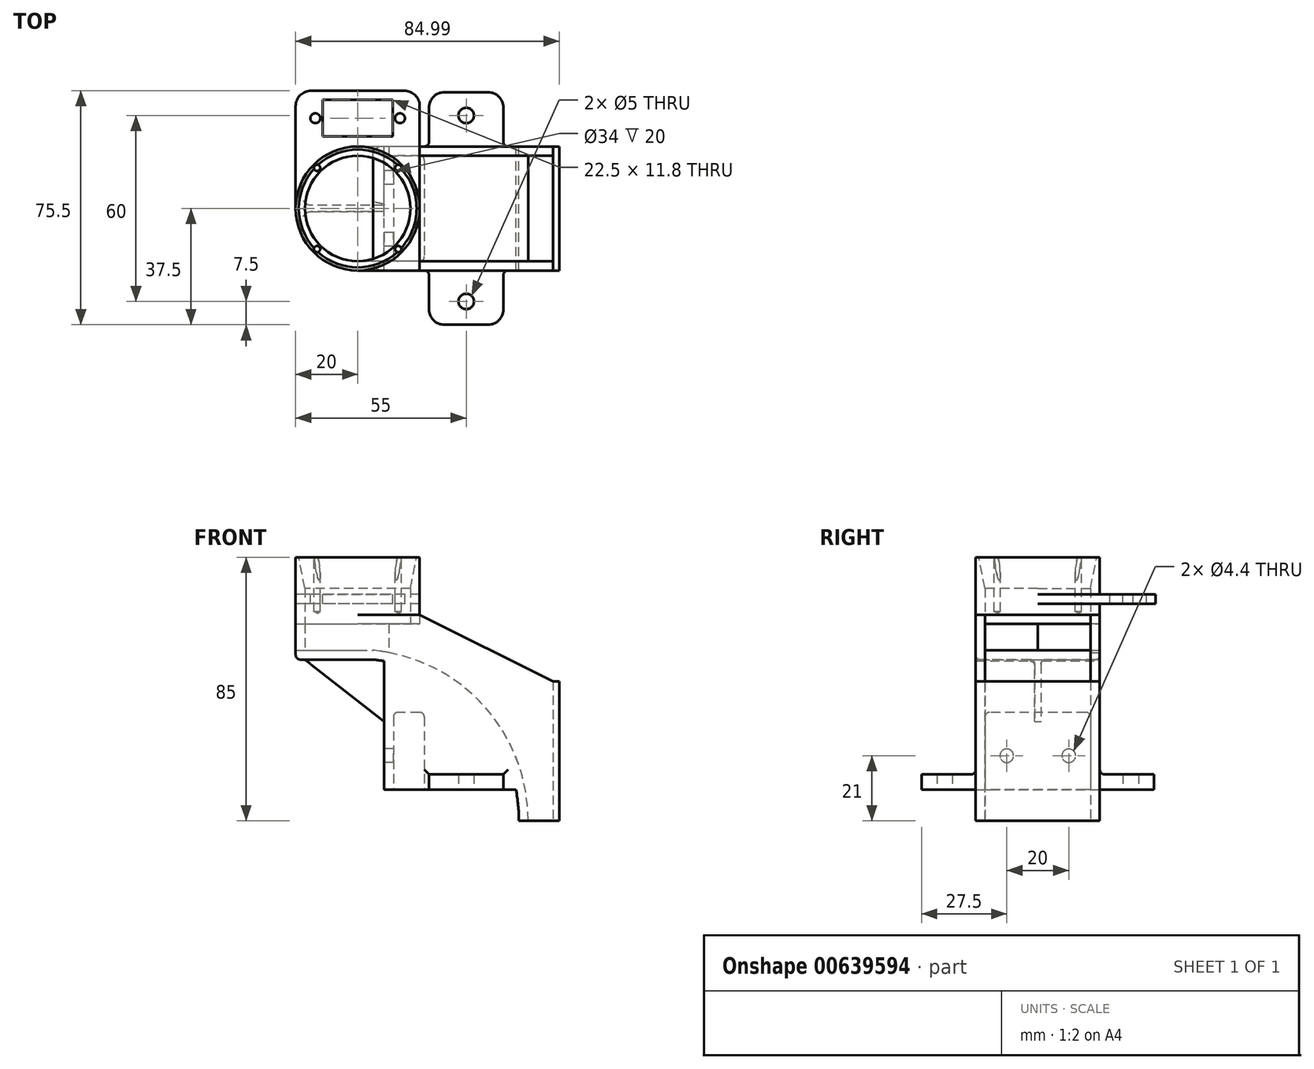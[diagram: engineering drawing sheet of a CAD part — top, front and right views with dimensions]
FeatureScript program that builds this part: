
annotation { "Feature Type Name" : "Feature", "Feature Type Description" : "" }
export const myFeature = defineFeature(function(context is Context, id is Id, definition is map)
    precondition{}
    {
        {
            var Q0;
            Q0=qCreatedBy(makeId("Top.planeOp"),FACE);
            var sketch = newSketch(context, id + "F0", { "sketchPlane" : qUnion([Q0])});
            skCircle(sketch, "E0", {"center": v(0, 0) * mm, "radius": 17 * mm});
            skCircle(sketch, "E1", {"center": v(0, 0) * mm, "radius": 20 * mm});
            skSolve(sketch);
        }
        {
            var Q0;
            Q0 = qSketchRegion(id + "F0", true);
            extrude(context, id + "F1", {"entities" : qUnion([Q0]), "depth" : 30 * mm, "offsetDistance" : 25 * mm});
        }
        {
            var Q0;
            Q0=makeQuery(id+"F1.opExtrude","CAP_EDGE",EDGE,{"disambiguationData":[OSD([sQuery(id+"F0.wireOp",EDGE,"E0")])],"isStart":false});
            chamfer(context, id + "F2", {"entities" : qUnion([Q0]), "chamferType" : ChamferType.TWO_OFFSETS, "width1" : 10 * mm, "oppositeDirection" : false, "width2" : 2 * mm, "tangentPropagation" : true});
        }
        {
            var Q0;
            Q0=makeQuery(id+"F1.opExtrude","CAP_FACE",FACE,{"disambiguationData":[OSD([sQuery(id+"F0.wireOp",EDGE,"E0"),sQuery(id+"F0.wireOp",EDGE,"E1")])],"isStart":false});
            var sketch = newSketch(context, id + "F3", { "sketchPlane" : qUnion([Q0])});
            skPoint(sketch, "E2", {"position": v(-13.08, -13.08) * mm});
            skLineSegment(sketch, "E3", {"start": v(-13.08, -13.08) * mm, "end": v(0, 0) * mm, "construction": true});
            skPoint(sketch, "E4", {"position": v(-13.08, 13.08) * mm});
            skLineSegment(sketch, "E5", {"start": v(-13.08, 13.08) * mm, "end": v(0, 0) * mm, "construction": true});
            skPoint(sketch, "E6", {"position": v(13.08, 13.08) * mm});
            skPoint(sketch, "E7", {"position": v(13.08, -13.08) * mm});
            skLineSegment(sketch, "E8", {"start": v(13.08, -13.08) * mm, "end": v(0, 0) * mm, "construction": true});
            skLineSegment(sketch, "E9", {"start": v(0, 0) * mm, "end": v(13.08, 13.08) * mm, "construction": true});
            skSolve(sketch);
        }
        {
            var Q0;
            Q0=sQuery(id+"F3.wireOp",VERTEX,"E4");
            var Q1;
            Q1=sQuery(id+"F3.wireOp",VERTEX,"E2");
            var Q2;
            Q2=sQuery(id+"F3.wireOp",VERTEX,"E7");
            var Q3;
            Q3=sQuery(id+"F3.wireOp",VERTEX,"E6");
            var Q4;
            Q4=makeQuery(id+"F1.opExtrude","SWEPT_BODY",BODY,{"disambiguationData":[OSD([sQuery(id+"F0.wireOp",EDGE,"E0"),sQuery(id+"F0.wireOp",EDGE,"E1")])]});
            hole(context, id + "F4", {"style" : HoleStyle.SIMPLE, "endStyle" : HoleEndStyle.BLIND, "holeDiameter" : 2 * mm, "majorDiameter" : 5 * mm, "holeDepth" : 10 * mm, "isTappedThrough" : true, "tappedDepth" : 12 * mm, "tapClearance" : 3, "locations" : qUnion([Q0, Q1, Q2, Q3]), "scope" : qUnion([Q4])});
        }
        {
            var Q0;
            Q0=makeQuery(id+"F1.opExtrude","CAP_FACE",FACE,{"disambiguationData":[OSD([sQuery(id+"F0.wireOp",EDGE,"E0"),sQuery(id+"F0.wireOp",EDGE,"E1")])],"isStart":true});
            var sketch = newSketch(context, id + "F5", { "sketchPlane" : qUnion([Q0])});
            skLineSegment(sketch, "E10", {"start": v(-20, 0) * mm, "end": v(0, 0) * mm});
            skLineSegment(sketch, "E11", {"start": v(0, 0) * mm, "end": v(0, 20) * mm});
            skLineSegment(sketch, "E12", {"start": v(0, 20) * mm, "end": v(20, 20) * mm});
            skLineSegment(sketch, "E13", {"start": v(20, 20) * mm, "end": v(20, -20) * mm});
            skLineSegment(sketch, "E14", {"start": v(20, -20) * mm, "end": v(-20, -20) * mm});
            skLineSegment(sketch, "E15", {"start": v(-20, -20) * mm, "end": v(-20, 0) * mm});
            skSolve(sketch);
        }
        {
            var Q0;
            Q0 = qSketchRegion(id + "F5", true);
            extrude(context, id + "F6", {"entities" : qUnion([Q0]), "operationType" : NewBodyOperationType.REMOVE, "oppositeDirection" : true, "depth" : 8.5 * mm, "offsetDistance" : 25 * mm});
        }
        {
            var Q0;
            Q0=makeQuery(id+"F6.boolean.opBoolean","COPY",FACE,{"derivedFrom":makeQuery(id+"F6.opExtrude","CAP_FACE",FACE,{"disambiguationData":[OSD([sQuery(id+"F5.wireOp",EDGE,"E10"),sQuery(id+"F5.wireOp",EDGE,"E11"),sQuery(id+"F5.wireOp",EDGE,"E12"),sQuery(id+"F5.wireOp",EDGE,"E13"),sQuery(id+"F5.wireOp",EDGE,"E14"),sQuery(id+"F5.wireOp",EDGE,"E15")])],"isStart":false})});
            var sketch = newSketch(context, id + "F7", { "sketchPlane" : qUnion([Q0])});
            skLineSegment(sketch, "E16", {"start": v(0, 20) * mm, "end": v(20, 20) * mm});
            skLineSegment(sketch, "E17", {"start": v(20, 20) * mm, "end": v(20, -20) * mm});
            skLineSegment(sketch, "E18", {"start": v(20, -20) * mm, "end": v(0, -20) * mm});
            skArc(sketch, "E19", {"start": v(0, -20) * mm, "mid": v(20, 0) * mm, "end": v(0, 20) * mm});
            skSolve(sketch);
        }
        {
            var Q0;
            Q0 = qSketchRegion(id + "F7", true);
            extrude(context, id + "F8", {"entities" : qUnion([Q0]), "operationType" : NewBodyOperationType.ADD, "oppositeDirection" : true, "depth" : 3 * mm, "offsetDistance" : 25 * mm});
        }
        {
            var Q0;
            Q0=makeQuery(id+"F1.opExtrude","CAP_FACE",FACE,{"disambiguationData":[OSD([sQuery(id+"F0.wireOp",EDGE,"E0"),sQuery(id+"F0.wireOp",EDGE,"E1")])],"isStart":true});
            var sketch = newSketch(context, id + "F9", { "sketchPlane" : qUnion([Q0])});
            skArc(sketch, "E20", {"start": v(0, 20) * mm, "mid": v(-20, 0) * mm, "end": v(0, -20) * mm});
            skLineSegment(sketch, "E21", {"start": v(0, 20) * mm, "end": v(5, 20) * mm});
            skLineSegment(sketch, "E22", {"start": v(5, 20) * mm, "end": v(5, -20) * mm});
            skLineSegment(sketch, "E23", {"start": v(5, -20) * mm, "end": v(0, -20) * mm});
            skSolve(sketch);
        }
        {
            var Q0;
            Q0 = qSketchRegion(id + "F9", true);
            extrude(context, id + "F10", {"entities" : qUnion([Q0]), "operationType" : NewBodyOperationType.ADD, "depth" : 3 * mm, "offsetDistance" : 25 * mm});
        }
        {
            var Q0;
            Q0=qCreatedBy(makeId("Front.planeOp"),FACE);
            var sketch = newSketch(context, id + "F11", { "sketchPlane" : qUnion([Q0])});
            skLineSegment(sketch, "E24", {"start": v(5, 0) * mm, "end": v(5, -3) * mm});
            skArc(sketch, "E25", {"start": v(54.99, -55) * mm, "mid": v(40.62, -17.84) * mm, "end": v(5, 0) * mm});
            skArc(sketch, "E26", {"start": v(52, -55) * mm, "mid": v(38.5, -19.95) * mm, "end": v(5, -3) * mm});
            skLineSegment(sketch, "E27", {"start": v(52, -55) * mm, "end": v(54.99, -55) * mm});
            skSolve(sketch);
        }
        {
            var Q0;
            Q0 = qSketchRegion(id + "F11", true);
            var Q1;
            Q1=makeQuery(id+"F8.opExtrude","SWEPT_FACE",FACE,{"disambiguationData":[OSD([sQuery(id+"F7.wireOp",EDGE,"E16")])]});
            var Q2;
            Q2=makeQuery(id+"F8.opExtrude","SWEPT_FACE",FACE,{"disambiguationData":[OSD([sQuery(id+"F7.wireOp",EDGE,"E18")])]});
            extrude(context, id + "F12", {"entities" : qUnion([Q0]), "operationType" : NewBodyOperationType.ADD, "endBound" : BoundingType.UP_TO_SURFACE, "depth" : 9.5 * mm, "endBoundEntityFace" : qUnion([Q1]), "offsetDistance" : 25 * mm, "hasSecondDirection" : true, "secondDirectionBound" : BoundingType.UP_TO_SURFACE, "secondDirectionOppositeDirection" : true, "secondDirectionDepth" : 9.5 * mm, "secondDirectionBoundEntityFace" : qUnion([Q2])});
        }
        {
            var Q0;
            Q0=makeQuery(id+"F8.opExtrude","SWEPT_FACE",FACE,{"disambiguationData":[OSD([sQuery(id+"F7.wireOp",EDGE,"E16")])]});
            var sketch = newSketch(context, id + "F13", { "sketchPlane" : qUnion([Q0])});
            skLineSegment(sketch, "E28", {"start": v(0, 11.5) * mm, "end": v(0, 0) * mm});
            skLineSegment(sketch, "E29", {"start": v(0, 0) * mm, "end": v(5, 0) * mm});
            skLineSegment(sketch, "E30", {"start": v(0, 11.5) * mm, "end": v(20, 11.5) * mm});
            skLineSegment(sketch, "E31", {"start": v(20, 11.5) * mm, "end": v(62.99, -10) * mm});
            skLineSegment(sketch, "E32", {"start": v(62.99, -10) * mm, "end": v(62.99, -55) * mm});
            skLineSegment(sketch, "E33", {"start": v(62.99, -55) * mm, "end": v(54.99, -55) * mm});
            skArc(sketch, "E34", {"start": v(54.99, -55) * mm, "mid": v(40.62, -17.84) * mm, "end": v(5, 0) * mm});
            skSolve(sketch);
        }
        {
            var Q0;
            Q0 = qSketchRegion(id + "F13", true);
            extrude(context, id + "F14", {"entities" : qUnion([Q0]), "operationType" : NewBodyOperationType.ADD, "oppositeDirection" : true, "depth" : 3 * mm, "offsetDistance" : 25 * mm});
        }
        {
            var Q0;
            Q0=makeQuery(id+"F8.opExtrude","SWEPT_FACE",FACE,{"disambiguationData":[OSD([sQuery(id+"F7.wireOp",EDGE,"E18")])]});
            var sketch = newSketch(context, id + "F15", { "sketchPlane" : qUnion([Q0])});
            skLineSegment(sketch, "E35", {"start": v(-62.99, -55) * mm, "end": v(-54.99, -55) * mm});
            skArc(sketch, "E36", {"start": v(-10, -0.71) * mm, "mid": v(-42.28, -19.75) * mm, "end": v(-54.99, -55) * mm});
            skLineSegment(sketch, "E37.0", {"start": v(-20, 11.5) * mm, "end": v(-62.99, -10) * mm});
            skLineSegment(sketch, "E38.0.0", {"start": v(-62.99, -10) * mm, "end": v(-62.99, -55) * mm});
            skLineSegment(sketch, "E38.0.2", {"start": v(-62.99, -55) * mm, "end": v(-62.99, -10) * mm});
            skLineSegment(sketch, "E39", {"start": v(-20, 11.5) * mm, "end": v(-20, 11.5) * mm});
            skLineSegment(sketch, "E40", {"start": v(-20, 11.5) * mm, "end": v(-10, 11.5) * mm});
            skLineSegment(sketch, "E41", {"start": v(-10, 11.5) * mm, "end": v(-10, -0.71) * mm});
            skSolve(sketch);
        }
        {
            var Q0;
            Q0 = qSketchRegion(id + "F15", true);
            extrude(context, id + "F16", {"entities" : qUnion([Q0]), "operationType" : NewBodyOperationType.ADD, "oppositeDirection" : true, "depth" : 3 * mm, "offsetDistance" : 25 * mm});
        }
        {
            var Q0;
            Q0=qCreatedBy(makeId("Front.planeOp"),FACE);
            var sketch = newSketch(context, id + "F17", { "sketchPlane" : qUnion([Q0])});
            skLineSegment(sketch, "E42", {"start": v(62.99, -55) * mm, "end": v(64.99, -55) * mm});
            skLineSegment(sketch, "E43", {"start": v(64.99, -55) * mm, "end": v(64.99, -10) * mm});
            skLineSegment(sketch, "E44", {"start": v(64.99, -10) * mm, "end": v(62.99, -10) * mm});
            skLineSegment(sketch, "E45", {"start": v(62.99, -10) * mm, "end": v(62.99, -55) * mm});
            skSolve(sketch);
        }
        {
            var Q0;
            Q0 = qSketchRegion(id + "F17", true);
            var Q1;
            {var subQ0=sQuery(id+"F7.wireOp",EDGE,"E16");Q1=makeQuery(id+"F14.boolean.opBoolean","MERGE",FACE,{"derivedFrom":[makeQuery(id+"F8.opExtrude","SWEPT_FACE",FACE,{"disambiguationData":[OSD([subQ0])]}),makeQuery(id+"F12.boolean.opBoolean","MERGE",FACE,{"derivedFrom":[makeQuery(id+"F10.opExtrude","SWEPT_FACE",FACE,{"disambiguationData":[OSD([sQuery(id+"F9.wireOp",EDGE,"E21")])]}),makeQuery(id+"F12.opExtrude","CAP_FACE",FACE,{"disambiguationData":[OSD([subQ0])],"isStart":false})]}),makeQuery(id+"F14.opExtrude","CAP_FACE",FACE,{"disambiguationData":[OSD([sQuery(id+"F13.wireOp",EDGE,"E28"),sQuery(id+"F13.wireOp",EDGE,"E29"),sQuery(id+"F13.wireOp",EDGE,"E30"),sQuery(id+"F13.wireOp",EDGE,"E31"),sQuery(id+"F13.wireOp",EDGE,"E32"),sQuery(id+"F13.wireOp",EDGE,"E33"),sQuery(id+"F13.wireOp",EDGE,"E34")])],"isStart":true})]});}
            var Q2;
            {var subQ0=sQuery(id+"F7.wireOp",EDGE,"E18");Q2=makeQuery(id+"F16.boolean.opBoolean","MERGE",FACE,{"derivedFrom":[makeQuery(id+"F8.opExtrude","SWEPT_FACE",FACE,{"disambiguationData":[OSD([subQ0])]}),makeQuery(id+"F12.boolean.opBoolean","MERGE",FACE,{"derivedFrom":[makeQuery(id+"F10.opExtrude","SWEPT_FACE",FACE,{"disambiguationData":[OSD([sQuery(id+"F9.wireOp",EDGE,"E23")])]}),makeQuery(id+"F12.opExtrude","CAP_FACE",FACE,{"disambiguationData":[OSD([subQ0])],"isStart":true})]}),makeQuery(id+"F16.opExtrude","CAP_FACE",FACE,{"disambiguationData":[OSD([sQuery(id+"F15.wireOp",EDGE,"RuU302Il-1nru-g0b3-ctYl-8AV5KIJRYzor"),sQuery(id+"F15.wireOp",EDGE,"kwzLpJch-1ExY-UgHB-C4fC-gWMRAG2XTcAg"),sQuery(id+"F15.wireOp",EDGE,"E35"),sQuery(id+"F15.wireOp",EDGE,"E36"),sQuery(id+"F15.wireOp",EDGE,"uAtuuOPQ-Y4R9-PvW4-TTvW-OnEqOC83DOFm")])],"isStart":true})]});}
            extrude(context, id + "F18", {"entities" : qUnion([Q0]), "operationType" : NewBodyOperationType.ADD, "endBound" : BoundingType.UP_TO_SURFACE, "depth" : 9.5 * mm, "endBoundEntityFace" : qUnion([Q1]), "offsetDistance" : 25 * mm, "hasSecondDirection" : true, "secondDirectionBound" : BoundingType.UP_TO_SURFACE, "secondDirectionOppositeDirection" : true, "secondDirectionDepth" : 9.5 * mm, "secondDirectionBoundEntityFace" : qUnion([Q2])});
        }
        {
            var Q0;
            Q0=qCreatedBy(makeId("Front.planeOp"),FACE);
            var sketch = newSketch(context, id + "F19", { "sketchPlane" : qUnion([Q0])});
            skArc(sketch, "E46", {"start": v(51.03, -45) * mm, "mid": v(36.25, -17.6) * mm, "end": v(8.5, -3.47) * mm});
            skLineSegment(sketch, "E47", {"start": v(51.03, -45) * mm, "end": v(8.5, -45) * mm});
            skLineSegment(sketch, "E48", {"start": v(8.5, -3.47) * mm, "end": v(8.5, -45) * mm});
            skSolve(sketch);
        }
        {
            var Q0;
            Q0 = qSketchRegion(id + "F19", true);
            var Q1;
            {var subQ0=sQuery(id+"F13.wireOp",EDGE,"E34");var subQ1=sQuery(id+"F13.wireOp",EDGE,"E33");var subQ2=sQuery(id+"F13.wireOp",EDGE,"E32");var subQ3=sQuery(id+"F13.wireOp",EDGE,"E31");var subQ4=sQuery(id+"F13.wireOp",EDGE,"E30");var subQ5=sQuery(id+"F13.wireOp",EDGE,"E29");var subQ6=sQuery(id+"F13.wireOp",EDGE,"E28");var subQ7=sQuery(id+"F9.wireOp",EDGE,"E21");var subQ8=sQuery(id+"F7.wireOp",EDGE,"E16");Q1=makeQuery(id+"F18.boolean.opBoolean","MERGE",FACE,{"derivedFrom":[makeQuery(id+"F14.boolean.opBoolean","MERGE",FACE,{"derivedFrom":[makeQuery(id+"F8.opExtrude","SWEPT_FACE",FACE,{"disambiguationData":[OSD([subQ8])]}),makeQuery(id+"F12.boolean.opBoolean","MERGE",FACE,{"derivedFrom":[makeQuery(id+"F10.opExtrude","SWEPT_FACE",FACE,{"disambiguationData":[OSD([subQ7])]}),makeQuery(id+"F12.opExtrude","CAP_FACE",FACE,{"disambiguationData":[OSD([subQ8])],"isStart":false})]}),makeQuery(id+"F14.opExtrude","CAP_FACE",FACE,{"disambiguationData":[OSD([subQ6,subQ5,subQ4,subQ3,subQ2,subQ1,subQ0])],"isStart":true})]}),makeQuery(id+"F18.opExtrude","CAP_FACE",FACE,{"disambiguationData":[OSD([subQ8,subQ7,subQ6,subQ5,subQ4,subQ3,subQ2,subQ1,subQ0])],"isStart":false})]});}
            var Q2;
            {var subQ0=sQuery(id+"F15.wireOp",EDGE,"uAtuuOPQ-Y4R9-PvW4-TTvW-OnEqOC83DOFm");var subQ1=sQuery(id+"F15.wireOp",EDGE,"E36");var subQ2=sQuery(id+"F15.wireOp",EDGE,"E35");var subQ3=sQuery(id+"F15.wireOp",EDGE,"kwzLpJch-1ExY-UgHB-C4fC-gWMRAG2XTcAg");var subQ4=sQuery(id+"F15.wireOp",EDGE,"RuU302Il-1nru-g0b3-ctYl-8AV5KIJRYzor");var subQ5=sQuery(id+"F9.wireOp",EDGE,"E23");var subQ6=sQuery(id+"F7.wireOp",EDGE,"E18");Q2=makeQuery(id+"F18.boolean.opBoolean","MERGE",FACE,{"derivedFrom":[makeQuery(id+"F16.boolean.opBoolean","MERGE",FACE,{"derivedFrom":[makeQuery(id+"F8.opExtrude","SWEPT_FACE",FACE,{"disambiguationData":[OSD([subQ6])]}),makeQuery(id+"F12.boolean.opBoolean","MERGE",FACE,{"derivedFrom":[makeQuery(id+"F10.opExtrude","SWEPT_FACE",FACE,{"disambiguationData":[OSD([subQ5])]}),makeQuery(id+"F12.opExtrude","CAP_FACE",FACE,{"disambiguationData":[OSD([subQ6])],"isStart":true})]}),makeQuery(id+"F16.opExtrude","CAP_FACE",FACE,{"disambiguationData":[OSD([subQ4,subQ3,subQ2,subQ1,subQ0])],"isStart":true})]}),makeQuery(id+"F18.opExtrude","CAP_FACE",FACE,{"disambiguationData":[OSD([subQ6,subQ5,subQ4,subQ3,subQ2,subQ1,subQ0])],"isStart":true})]});}
            extrude(context, id + "F20", {"entities" : qUnion([Q0]), "operationType" : NewBodyOperationType.ADD, "endBound" : BoundingType.UP_TO_SURFACE, "depth" : 25 * mm, "endBoundEntityFace" : qUnion([Q1]), "offsetDistance" : 25 * mm, "hasSecondDirection" : true, "secondDirectionBound" : BoundingType.UP_TO_SURFACE, "secondDirectionOppositeDirection" : true, "secondDirectionDepth" : 25 * mm, "secondDirectionBoundEntityFace" : qUnion([Q2])});
        }
        {
            var Q0;
            Q0=qCreatedBy(makeId("Top.planeOp"),FACE);
            cPlane(context, id + "F21", {"entities" : qUnion([Q0]), "cplaneType" : CPlaneType.OFFSET, "offset" : 15 * mm, "width" : 150 * mm, "height" : 150 * mm});
        }
        {
            var Q0;
            Q0=makeQuery(id+"F20.opExtrude","SWEPT_FACE",FACE,{"disambiguationData":[OSD([sQuery(id+"F19.wireOp",EDGE,"E47")])]});
            var sketch = newSketch(context, id + "F22", { "sketchPlane" : qUnion([Q0])});
            skLineSegment(sketch, "E49.bottom", {"start": v(47, -37.5) * mm, "end": v(23, -37.5) * mm});
            skLineSegment(sketch, "E49.top", {"start": v(47, 37.5) * mm, "end": v(23, 37.5) * mm});
            skLineSegment(sketch, "E49.left", {"start": v(47, -37.5) * mm, "end": v(47, 37.5) * mm});
            skLineSegment(sketch, "E49.right", {"start": v(23, -37.5) * mm, "end": v(23, 37.5) * mm});
            skPoint(sketch, "E49.middle", {"position": v(35, 0) * mm});
            skPoint(sketch, "E50", {"position": v(35, 30) * mm});
            skPoint(sketch, "E51.MirrorP", {"position": v(35, -30) * mm});
            skSolve(sketch);
        }
        {
            var Q0;
            Q0=qCreatedBy(id+"F21.planeOp",FACE);
            var sketch = newSketch(context, id + "F23", { "sketchPlane" : qUnion([Q0])});
            skLineSegment(sketch, "E52", {"start": v(20, 0) * mm, "end": v(20, 38) * mm});
            skLineSegment(sketch, "E53", {"start": v(20, 38) * mm, "end": v(0, 38) * mm});
            skArc(sketch, "E54", {"start": v(20, 0) * mm, "mid": v(14.14, 14.14) * mm, "end": v(0, 20) * mm});
            skLineSegment(sketch, "E55.MirrorCS", {"start": v(-20, 38) * mm, "end": v(0, 38) * mm});
            skLineSegment(sketch, "E56.MirrorCS", {"start": v(-20, 0) * mm, "end": v(-20, 38) * mm});
            skArc(sketch, "E57.MirrorCS", {"start": v(-20, 0) * mm, "mid": v(-14.14, 14.14) * mm, "end": v(0, 20) * mm});
            skSolve(sketch);
        }
        {
            var Q0;
            Q0 = qSketchRegion(id + "F23", true);
            extrude(context, id + "F24", {"entities" : qUnion([Q0]), "operationType" : NewBodyOperationType.ADD, "depth" : 3 * mm, "offsetDistance" : 25 * mm});
        }
        {
            var Q0;
            Q0=makeQuery(id+"F24.opExtrude","CAP_FACE",FACE,{"disambiguationData":[OSD([sQuery(id+"F23.wireOp",EDGE,"E52"),sQuery(id+"F23.wireOp",EDGE,"E53"),sQuery(id+"F23.wireOp",EDGE,"E54"),sQuery(id+"F23.wireOp",EDGE,"E55.MirrorCS"),sQuery(id+"F23.wireOp",EDGE,"E56.MirrorCS"),sQuery(id+"F23.wireOp",EDGE,"E57.MirrorCS")])],"isStart":false});
            var sketch = newSketch(context, id + "F25", { "sketchPlane" : qUnion([Q0])});
            skLineSegment(sketch, "E58.bottom", {"start": v(-11.25, 35) * mm, "end": v(11.25, 35) * mm});
            skLineSegment(sketch, "E58.top", {"start": v(-11.25, 23.2) * mm, "end": v(11.25, 23.2) * mm});
            skLineSegment(sketch, "E58.left", {"start": v(-11.25, 35) * mm, "end": v(-11.25, 23.2) * mm});
            skLineSegment(sketch, "E58.right", {"start": v(11.25, 35) * mm, "end": v(11.25, 23.2) * mm});
            skCircle(sketch, "E59", {"center": v(-13.65, 29.1) * mm, "radius": 1.6 * mm});
            skCircle(sketch, "E60.MirrorC", {"center": v(13.65, 29.1) * mm, "radius": 1.6 * mm});
            skSolve(sketch);
        }
        {
            var Q0;
            Q0 = qSketchRegion(id + "F25", true);
            extrude(context, id + "F26", {"entities" : qUnion([Q0]), "operationType" : NewBodyOperationType.REMOVE, "endBound" : BoundingType.UP_TO_NEXT, "oppositeDirection" : true, "depth" : 25 * mm, "offsetDistance" : 25 * mm});
        }
        {
            var Q0;
            Q0 = qSketchRegion(id + "F22", true);
            extrude(context, id + "F27", {"entities" : qUnion([Q0]), "operationType" : NewBodyOperationType.ADD, "oppositeDirection" : true, "depth" : 5 * mm, "offsetDistance" : 25 * mm});
        }
        {
            var Q0;
            Q0=sQuery(id+"F22.wireOp",VERTEX,"E50");
            var Q1;
            Q1=sQuery(id+"F22.wireOp",VERTEX,"E51.MirrorP");
            var Q2;
            Q2=makeQuery(id+"F1.opExtrude","SWEPT_BODY",BODY,{"disambiguationData":[OSD([sQuery(id+"F0.wireOp",EDGE,"E0"),sQuery(id+"F0.wireOp",EDGE,"E1")])]});
            hole(context, id + "F28", {"style" : HoleStyle.SIMPLE, "endStyle" : HoleEndStyle.THROUGH, "standardTappedOrClearance" : lookupTablePath({ "standard" : "ISO", "size" : "5", "type" : "Drilled" }), "standardBlindInLast" : lookupTablePath({ "standard" : "ISO", "size" : "5", "type" : "Drilled" }), "holeDiameter" : 5 * mm, "majorDiameter" : 5 * mm, "isTappedThrough" : true, "tappedDepth" : 12 * mm, "tapClearance" : 3, "locations" : qUnion([Q0, Q1]), "scope" : qUnion([Q2])});
        }
        {
            var Q0;
            Q0=qCreatedBy(makeId("Front.planeOp"),FACE);
            var sketch = newSketch(context, id + "F29", { "sketchPlane" : qUnion([Q0])});
            skLineSegment(sketch, "E61", {"start": v(-17, -3) * mm, "end": v(8.5, -3) * mm});
            skLineSegment(sketch, "E62", {"start": v(8.5, -3) * mm, "end": v(8.5, -23) * mm});
            skLineSegment(sketch, "E63", {"start": v(8.5, -23) * mm, "end": v(-17, -3) * mm});
            skSolve(sketch);
        }
        {
            var Q0;
            Q0 = qSketchRegion(id + "F29", true);
            extrude(context, id + "F30", {"entities" : qUnion([Q0]), "operationType" : NewBodyOperationType.ADD, "depth" : 2 * mm, "offsetDistance" : 25 * mm, "symmetric" : true});
        }
        {
            var Q0;
            Q0=makeQuery(id+"F27.opExtrude","SWEPT_EDGE",EDGE,{"disambiguationData":[OSD([sQuery(id+"F22.wireOp",EDGE,"E49.top"),sQuery(id+"F22.wireOp",EDGE,"E49.right")])]});
            var Q1;
            Q1=makeQuery(id+"F27.opExtrude","SWEPT_EDGE",EDGE,{"disambiguationData":[OSD([sQuery(id+"F22.wireOp",EDGE,"E49.top"),sQuery(id+"F22.wireOp",EDGE,"E49.left")])]});
            var Q2;
            Q2=makeQuery(id+"F27.opExtrude","SWEPT_EDGE",EDGE,{"disambiguationData":[OSD([sQuery(id+"F22.wireOp",EDGE,"E49.bottom"),sQuery(id+"F22.wireOp",EDGE,"E49.left")])]});
            var Q3;
            Q3=makeQuery(id+"F27.opExtrude","SWEPT_EDGE",EDGE,{"disambiguationData":[OSD([sQuery(id+"F22.wireOp",EDGE,"E49.bottom"),sQuery(id+"F22.wireOp",EDGE,"E49.right")])]});
            var Q4;
            Q4=makeQuery(id+"F24.opExtrude","SWEPT_EDGE",EDGE,{"disambiguationData":[OSD([sQuery(id+"F23.wireOp",EDGE,"E52"),sQuery(id+"F23.wireOp",EDGE,"E53")])]});
            var Q5;
            Q5=makeQuery(id+"F24.opExtrude","SWEPT_EDGE",EDGE,{"disambiguationData":[OSD([sQuery(id+"F23.wireOp",EDGE,"E55.MirrorCS"),sQuery(id+"F23.wireOp",EDGE,"E56.MirrorCS")])]});
            fillet(context, id + "F31", {"entities" : qUnion([Q0, Q1, Q2, Q3, Q4, Q5]), "radius" : 5 * mm, "tangentPropagation" : true, "allowEdgeOverflow" : false});
        }
        {
            var Q0;
            Q0=makeQuery(id+"F27.boolean.opBoolean","MERGE",FACE,{"derivedFrom":[makeQuery(id+"F20.opExtrude","SWEPT_FACE",FACE,{"disambiguationData":[OSD([sQuery(id+"F19.wireOp",EDGE,"E47")])]}),makeQuery(id+"F27.opExtrude","CAP_FACE",FACE,{"disambiguationData":[OSD([sQuery(id+"F22.wireOp",EDGE,"E49.bottom"),sQuery(id+"F22.wireOp",EDGE,"E49.top"),sQuery(id+"F22.wireOp",EDGE,"E49.left"),sQuery(id+"F22.wireOp",EDGE,"E49.right")])],"isStart":true})]});
            var sketch = newSketch(context, id + "F32", { "sketchPlane" : qUnion([Q0])});
            skLineSegment(sketch, "E64.bottom", {"start": v(21.5, -17) * mm, "end": v(11.5, -17) * mm});
            skLineSegment(sketch, "E64.top", {"start": v(21.5, 17) * mm, "end": v(11.5, 17) * mm});
            skLineSegment(sketch, "E64.left", {"start": v(21.5, -17) * mm, "end": v(21.5, 17) * mm});
            skLineSegment(sketch, "E64.right", {"start": v(11.5, -17) * mm, "end": v(11.5, 17) * mm});
            skPoint(sketch, "E64.middle", {"position": v(16.5, 0) * mm});
            skSolve(sketch);
        }
        {
            var Q0;
            Q0 = qSketchRegion(id + "F32", true);
            extrude(context, id + "F33", {"entities" : qUnion([Q0]), "operationType" : NewBodyOperationType.REMOVE, "oppositeDirection" : true, "depth" : 25 * mm, "offsetDistance" : 25 * mm});
        }
        {
            var Q0;
            Q0=makeQuery(id+"F24.opExtrude","CAP_EDGE",EDGE,{"disambiguationData":[OSD([sQuery(id+"F23.wireOp",EDGE,"E54"),sQuery(id+"F23.wireOp",EDGE,"E57.MirrorCS")])],"isStart":false});
            var Q1;
            Q1=makeQuery(id+"F24.opExtrude","CAP_EDGE",EDGE,{"disambiguationData":[OSD([sQuery(id+"F23.wireOp",EDGE,"E54"),sQuery(id+"F23.wireOp",EDGE,"E57.MirrorCS")])],"isStart":true});
            var Q2;
            {var subQ0=sQuery(id+"F7.wireOp",EDGE,"E19");Q2=makeQuery(id+"F8.opExtrude","CAP_EDGE",EDGE,{"disambiguationData":[OSD([subQ0]),TDD([makeQuery(id+"F7.imprint","IMPRINT",EDGE,{"disambiguationData":[TD([[makeQuery(id+"F7.imprint","INTERSECT",VERTEX,{"derivedFrom":[sQuery(id+"F7.wireOp",EDGE,"E17"),subQ0]}),-1.0]])],"derivedFrom":subQ0})])],"isStart":false});}
            var Q3;
            {var subQ0=sQuery(id+"F7.wireOp",EDGE,"E18");Q3=makeQuery(id+"F18.opExtrude","TWEAK_EDGE",EDGE,{"derivedFrom":[makeQuery(id+"F16.boolean.opBoolean","MERGE",FACE,{"derivedFrom":[makeQuery(id+"F8.opExtrude","SWEPT_FACE",FACE,{"disambiguationData":[OSD([subQ0])]}),makeQuery(id+"F12.boolean.opBoolean","MERGE",FACE,{"derivedFrom":[makeQuery(id+"F10.opExtrude","SWEPT_FACE",FACE,{"disambiguationData":[OSD([sQuery(id+"F9.wireOp",EDGE,"E23")])]}),makeQuery(id+"F12.opExtrude","CAP_FACE",FACE,{"disambiguationData":[OSD([subQ0])],"isStart":true})]}),makeQuery(id+"F16.opExtrude","CAP_FACE",FACE,{"disambiguationData":[OSD([sQuery(id+"F15.wireOp",EDGE,"E35"),sQuery(id+"F15.wireOp",EDGE,"E36"),sQuery(id+"F15.wireOp",EDGE,"uAtuuOPQ-Y4R9-PvW4-TTvW-OnEqOC83DOFm"),sQuery(id+"F15.wireOp",EDGE,"E37.0"),sQuery(id+"F15.wireOp",EDGE,"E38.0.2")])],"isStart":true})]}),makeQuery(id+"F17.imprint","IMPRINT",EDGE,{"derivedFrom":sQuery(id+"F17.wireOp",EDGE,"E43")})]});}
            var Q4;
            {var subQ0=sQuery(id+"F7.wireOp",EDGE,"E16");Q4=makeQuery(id+"F18.opExtrude","TWEAK_EDGE",EDGE,{"derivedFrom":[makeQuery(id+"F14.boolean.opBoolean","MERGE",FACE,{"derivedFrom":[makeQuery(id+"F8.opExtrude","SWEPT_FACE",FACE,{"disambiguationData":[OSD([subQ0])]}),makeQuery(id+"F12.boolean.opBoolean","MERGE",FACE,{"derivedFrom":[makeQuery(id+"F10.opExtrude","SWEPT_FACE",FACE,{"disambiguationData":[OSD([sQuery(id+"F9.wireOp",EDGE,"E21")])]}),makeQuery(id+"F12.opExtrude","CAP_FACE",FACE,{"disambiguationData":[OSD([subQ0])],"isStart":false})]}),makeQuery(id+"F14.opExtrude","CAP_FACE",FACE,{"disambiguationData":[OSD([sQuery(id+"F13.wireOp",EDGE,"E28"),sQuery(id+"F13.wireOp",EDGE,"E29"),sQuery(id+"F13.wireOp",EDGE,"E30"),sQuery(id+"F13.wireOp",EDGE,"E31"),sQuery(id+"F13.wireOp",EDGE,"E32"),sQuery(id+"F13.wireOp",EDGE,"E33"),sQuery(id+"F13.wireOp",EDGE,"E34")])],"isStart":true})]}),makeQuery(id+"F17.imprint","IMPRINT",EDGE,{"derivedFrom":sQuery(id+"F17.wireOp",EDGE,"E43")})]});}
            var Q5;
            {var subQ0=sQuery(id+"F15.wireOp",EDGE,"E38.0.2");var subQ1=sQuery(id+"F15.wireOp",EDGE,"E37.0");var subQ2=sQuery(id+"F15.wireOp",EDGE,"uAtuuOPQ-Y4R9-PvW4-TTvW-OnEqOC83DOFm");var subQ3=sQuery(id+"F15.wireOp",EDGE,"E36");var subQ4=sQuery(id+"F15.wireOp",EDGE,"E35");var subQ5=sQuery(id+"F9.wireOp",EDGE,"E23");var subQ6=sQuery(id+"F7.wireOp",EDGE,"E18");Q5=makeQuery(id+"F27.boolean.opBoolean","INTERSECT",EDGE,{"derivedFrom":[makeQuery(id+"F20.boolean.opBoolean","MERGE",FACE,{"derivedFrom":[makeQuery(id+"F18.boolean.opBoolean","MERGE",FACE,{"derivedFrom":[makeQuery(id+"F16.boolean.opBoolean","MERGE",FACE,{"derivedFrom":[makeQuery(id+"F8.opExtrude","SWEPT_FACE",FACE,{"disambiguationData":[OSD([subQ6])]}),makeQuery(id+"F12.boolean.opBoolean","MERGE",FACE,{"derivedFrom":[makeQuery(id+"F10.opExtrude","SWEPT_FACE",FACE,{"disambiguationData":[OSD([subQ5])]}),makeQuery(id+"F12.opExtrude","CAP_FACE",FACE,{"disambiguationData":[OSD([subQ6])],"isStart":true})]}),makeQuery(id+"F16.opExtrude","CAP_FACE",FACE,{"disambiguationData":[OSD([subQ4,subQ3,subQ2,subQ1,subQ0])],"isStart":true})]}),makeQuery(id+"F18.opExtrude","CAP_FACE",FACE,{"disambiguationData":[OSD([subQ6,subQ5,subQ4,subQ3,subQ2,subQ1,subQ0])],"isStart":true})]}),makeQuery(id+"F20.opExtrude","CAP_FACE",FACE,{"disambiguationData":[OSD([subQ6,subQ5,subQ4,subQ3,subQ2,subQ1,subQ0])],"isStart":true})]}),makeQuery(id+"F27.opExtrude","CAP_FACE",FACE,{"disambiguationData":[OSD([sQuery(id+"F22.wireOp",EDGE,"E49.bottom"),sQuery(id+"F22.wireOp",EDGE,"E49.top"),sQuery(id+"F22.wireOp",EDGE,"E49.left"),sQuery(id+"F22.wireOp",EDGE,"E49.right")])],"isStart":false})]});}
            var Q6;
            {var subQ0=sQuery(id+"F15.wireOp",EDGE,"E38.0.2");var subQ1=sQuery(id+"F15.wireOp",EDGE,"E37.0");var subQ2=sQuery(id+"F15.wireOp",EDGE,"uAtuuOPQ-Y4R9-PvW4-TTvW-OnEqOC83DOFm");var subQ3=sQuery(id+"F15.wireOp",EDGE,"E36");var subQ4=sQuery(id+"F15.wireOp",EDGE,"E35");var subQ5=sQuery(id+"F9.wireOp",EDGE,"E23");var subQ6=sQuery(id+"F7.wireOp",EDGE,"E18");Q6=makeQuery(id+"F27.boolean.opBoolean","INTERSECT",EDGE,{"derivedFrom":[makeQuery(id+"F20.boolean.opBoolean","MERGE",FACE,{"derivedFrom":[makeQuery(id+"F18.boolean.opBoolean","MERGE",FACE,{"derivedFrom":[makeQuery(id+"F16.boolean.opBoolean","MERGE",FACE,{"derivedFrom":[makeQuery(id+"F8.opExtrude","SWEPT_FACE",FACE,{"disambiguationData":[OSD([subQ6])]}),makeQuery(id+"F12.boolean.opBoolean","MERGE",FACE,{"derivedFrom":[makeQuery(id+"F10.opExtrude","SWEPT_FACE",FACE,{"disambiguationData":[OSD([subQ5])]}),makeQuery(id+"F12.opExtrude","CAP_FACE",FACE,{"disambiguationData":[OSD([subQ6])],"isStart":true})]}),makeQuery(id+"F16.opExtrude","CAP_FACE",FACE,{"disambiguationData":[OSD([subQ4,subQ3,subQ2,subQ1,subQ0])],"isStart":true})]}),makeQuery(id+"F18.opExtrude","CAP_FACE",FACE,{"disambiguationData":[OSD([subQ6,subQ5,subQ4,subQ3,subQ2,subQ1,subQ0])],"isStart":true})]}),makeQuery(id+"F20.opExtrude","CAP_FACE",FACE,{"disambiguationData":[OSD([subQ6,subQ5,subQ4,subQ3,subQ2,subQ1,subQ0])],"isStart":true})]}),makeQuery(id+"F27.opExtrude","SWEPT_FACE",FACE,{"disambiguationData":[OSD([sQuery(id+"F22.wireOp",EDGE,"E49.left")])]})]});}
            var Q7;
            {var subQ0=sQuery(id+"F15.wireOp",EDGE,"E38.0.2");var subQ1=sQuery(id+"F15.wireOp",EDGE,"E37.0");var subQ2=sQuery(id+"F15.wireOp",EDGE,"uAtuuOPQ-Y4R9-PvW4-TTvW-OnEqOC83DOFm");var subQ3=sQuery(id+"F15.wireOp",EDGE,"E36");var subQ4=sQuery(id+"F15.wireOp",EDGE,"E35");var subQ5=sQuery(id+"F9.wireOp",EDGE,"E23");var subQ6=sQuery(id+"F7.wireOp",EDGE,"E18");Q7=makeQuery(id+"F27.boolean.opBoolean","INTERSECT",EDGE,{"derivedFrom":[makeQuery(id+"F20.boolean.opBoolean","MERGE",FACE,{"derivedFrom":[makeQuery(id+"F18.boolean.opBoolean","MERGE",FACE,{"derivedFrom":[makeQuery(id+"F16.boolean.opBoolean","MERGE",FACE,{"derivedFrom":[makeQuery(id+"F8.opExtrude","SWEPT_FACE",FACE,{"disambiguationData":[OSD([subQ6])]}),makeQuery(id+"F12.boolean.opBoolean","MERGE",FACE,{"derivedFrom":[makeQuery(id+"F10.opExtrude","SWEPT_FACE",FACE,{"disambiguationData":[OSD([subQ5])]}),makeQuery(id+"F12.opExtrude","CAP_FACE",FACE,{"disambiguationData":[OSD([subQ6])],"isStart":true})]}),makeQuery(id+"F16.opExtrude","CAP_FACE",FACE,{"disambiguationData":[OSD([subQ4,subQ3,subQ2,subQ1,subQ0])],"isStart":true})]}),makeQuery(id+"F18.opExtrude","CAP_FACE",FACE,{"disambiguationData":[OSD([subQ6,subQ5,subQ4,subQ3,subQ2,subQ1,subQ0])],"isStart":true})]}),makeQuery(id+"F20.opExtrude","CAP_FACE",FACE,{"disambiguationData":[OSD([subQ6,subQ5,subQ4,subQ3,subQ2,subQ1,subQ0])],"isStart":true})]}),makeQuery(id+"F27.opExtrude","SWEPT_FACE",FACE,{"disambiguationData":[OSD([sQuery(id+"F22.wireOp",EDGE,"E49.right")])]})]});}
            var Q8;
            {var subQ0=sQuery(id+"F13.wireOp",EDGE,"E34");var subQ1=sQuery(id+"F13.wireOp",EDGE,"E33");var subQ2=sQuery(id+"F13.wireOp",EDGE,"E32");var subQ3=sQuery(id+"F13.wireOp",EDGE,"E31");var subQ4=sQuery(id+"F13.wireOp",EDGE,"E30");var subQ5=sQuery(id+"F13.wireOp",EDGE,"E29");var subQ6=sQuery(id+"F13.wireOp",EDGE,"E28");var subQ7=sQuery(id+"F9.wireOp",EDGE,"E21");var subQ8=sQuery(id+"F7.wireOp",EDGE,"E16");Q8=makeQuery(id+"F27.boolean.opBoolean","INTERSECT",EDGE,{"derivedFrom":[makeQuery(id+"F20.boolean.opBoolean","MERGE",FACE,{"derivedFrom":[makeQuery(id+"F18.boolean.opBoolean","MERGE",FACE,{"derivedFrom":[makeQuery(id+"F14.boolean.opBoolean","MERGE",FACE,{"derivedFrom":[makeQuery(id+"F8.opExtrude","SWEPT_FACE",FACE,{"disambiguationData":[OSD([subQ8])]}),makeQuery(id+"F12.boolean.opBoolean","MERGE",FACE,{"derivedFrom":[makeQuery(id+"F10.opExtrude","SWEPT_FACE",FACE,{"disambiguationData":[OSD([subQ7])]}),makeQuery(id+"F12.opExtrude","CAP_FACE",FACE,{"disambiguationData":[OSD([subQ8])],"isStart":false})]}),makeQuery(id+"F14.opExtrude","CAP_FACE",FACE,{"disambiguationData":[OSD([subQ6,subQ5,subQ4,subQ3,subQ2,subQ1,subQ0])],"isStart":true})]}),makeQuery(id+"F18.opExtrude","CAP_FACE",FACE,{"disambiguationData":[OSD([subQ8,subQ7,subQ6,subQ5,subQ4,subQ3,subQ2,subQ1,subQ0])],"isStart":false})]}),makeQuery(id+"F20.opExtrude","CAP_FACE",FACE,{"disambiguationData":[OSD([subQ8,subQ7,subQ6,subQ5,subQ4,subQ3,subQ2,subQ1,subQ0])],"isStart":false})]}),makeQuery(id+"F27.opExtrude","SWEPT_FACE",FACE,{"disambiguationData":[OSD([sQuery(id+"F22.wireOp",EDGE,"E49.right")])]})]});}
            var Q9;
            {var subQ0=sQuery(id+"F13.wireOp",EDGE,"E34");var subQ1=sQuery(id+"F13.wireOp",EDGE,"E33");var subQ2=sQuery(id+"F13.wireOp",EDGE,"E32");var subQ3=sQuery(id+"F13.wireOp",EDGE,"E31");var subQ4=sQuery(id+"F13.wireOp",EDGE,"E30");var subQ5=sQuery(id+"F13.wireOp",EDGE,"E29");var subQ6=sQuery(id+"F13.wireOp",EDGE,"E28");var subQ7=sQuery(id+"F9.wireOp",EDGE,"E21");var subQ8=sQuery(id+"F7.wireOp",EDGE,"E16");Q9=makeQuery(id+"F27.boolean.opBoolean","INTERSECT",EDGE,{"derivedFrom":[makeQuery(id+"F20.boolean.opBoolean","MERGE",FACE,{"derivedFrom":[makeQuery(id+"F18.boolean.opBoolean","MERGE",FACE,{"derivedFrom":[makeQuery(id+"F14.boolean.opBoolean","MERGE",FACE,{"derivedFrom":[makeQuery(id+"F8.opExtrude","SWEPT_FACE",FACE,{"disambiguationData":[OSD([subQ8])]}),makeQuery(id+"F12.boolean.opBoolean","MERGE",FACE,{"derivedFrom":[makeQuery(id+"F10.opExtrude","SWEPT_FACE",FACE,{"disambiguationData":[OSD([subQ7])]}),makeQuery(id+"F12.opExtrude","CAP_FACE",FACE,{"disambiguationData":[OSD([subQ8])],"isStart":false})]}),makeQuery(id+"F14.opExtrude","CAP_FACE",FACE,{"disambiguationData":[OSD([subQ6,subQ5,subQ4,subQ3,subQ2,subQ1,subQ0])],"isStart":true})]}),makeQuery(id+"F18.opExtrude","CAP_FACE",FACE,{"disambiguationData":[OSD([subQ8,subQ7,subQ6,subQ5,subQ4,subQ3,subQ2,subQ1,subQ0])],"isStart":false})]}),makeQuery(id+"F20.opExtrude","CAP_FACE",FACE,{"disambiguationData":[OSD([subQ8,subQ7,subQ6,subQ5,subQ4,subQ3,subQ2,subQ1,subQ0])],"isStart":false})]}),makeQuery(id+"F27.opExtrude","CAP_FACE",FACE,{"disambiguationData":[OSD([sQuery(id+"F22.wireOp",EDGE,"E49.bottom"),sQuery(id+"F22.wireOp",EDGE,"E49.top"),sQuery(id+"F22.wireOp",EDGE,"E49.left"),sQuery(id+"F22.wireOp",EDGE,"E49.right")])],"isStart":false})]});}
            var Q10;
            {var subQ0=sQuery(id+"F13.wireOp",EDGE,"E34");var subQ1=sQuery(id+"F13.wireOp",EDGE,"E33");var subQ2=sQuery(id+"F13.wireOp",EDGE,"E32");var subQ3=sQuery(id+"F13.wireOp",EDGE,"E31");var subQ4=sQuery(id+"F13.wireOp",EDGE,"E30");var subQ5=sQuery(id+"F13.wireOp",EDGE,"E29");var subQ6=sQuery(id+"F13.wireOp",EDGE,"E28");var subQ7=sQuery(id+"F9.wireOp",EDGE,"E21");var subQ8=sQuery(id+"F7.wireOp",EDGE,"E16");Q10=makeQuery(id+"F27.boolean.opBoolean","INTERSECT",EDGE,{"derivedFrom":[makeQuery(id+"F20.boolean.opBoolean","MERGE",FACE,{"derivedFrom":[makeQuery(id+"F18.boolean.opBoolean","MERGE",FACE,{"derivedFrom":[makeQuery(id+"F14.boolean.opBoolean","MERGE",FACE,{"derivedFrom":[makeQuery(id+"F8.opExtrude","SWEPT_FACE",FACE,{"disambiguationData":[OSD([subQ8])]}),makeQuery(id+"F12.boolean.opBoolean","MERGE",FACE,{"derivedFrom":[makeQuery(id+"F10.opExtrude","SWEPT_FACE",FACE,{"disambiguationData":[OSD([subQ7])]}),makeQuery(id+"F12.opExtrude","CAP_FACE",FACE,{"disambiguationData":[OSD([subQ8])],"isStart":false})]}),makeQuery(id+"F14.opExtrude","CAP_FACE",FACE,{"disambiguationData":[OSD([subQ6,subQ5,subQ4,subQ3,subQ2,subQ1,subQ0])],"isStart":true})]}),makeQuery(id+"F18.opExtrude","CAP_FACE",FACE,{"disambiguationData":[OSD([subQ8,subQ7,subQ6,subQ5,subQ4,subQ3,subQ2,subQ1,subQ0])],"isStart":false})]}),makeQuery(id+"F20.opExtrude","CAP_FACE",FACE,{"disambiguationData":[OSD([subQ8,subQ7,subQ6,subQ5,subQ4,subQ3,subQ2,subQ1,subQ0])],"isStart":false})]}),makeQuery(id+"F27.opExtrude","SWEPT_FACE",FACE,{"disambiguationData":[OSD([sQuery(id+"F22.wireOp",EDGE,"E49.left")])]})]});}
            var Q11;
            {var subQ0=sQuery(id+"F13.wireOp",EDGE,"E34");var subQ1=sQuery(id+"F13.wireOp",EDGE,"E33");var subQ2=sQuery(id+"F13.wireOp",EDGE,"E32");var subQ3=sQuery(id+"F13.wireOp",EDGE,"E31");var subQ4=sQuery(id+"F13.wireOp",EDGE,"E30");var subQ5=sQuery(id+"F13.wireOp",EDGE,"E29");var subQ6=sQuery(id+"F13.wireOp",EDGE,"E28");var subQ7=sQuery(id+"F9.wireOp",EDGE,"E21");var subQ8=sQuery(id+"F7.wireOp",EDGE,"E16");Q11=makeQuery(id+"F20.opExtrude","TWEAK_EDGE",EDGE,{"derivedFrom":[makeQuery(id+"F18.boolean.opBoolean","MERGE",FACE,{"derivedFrom":[makeQuery(id+"F14.boolean.opBoolean","MERGE",FACE,{"derivedFrom":[makeQuery(id+"F8.opExtrude","SWEPT_FACE",FACE,{"disambiguationData":[OSD([subQ8])]}),makeQuery(id+"F12.boolean.opBoolean","MERGE",FACE,{"derivedFrom":[makeQuery(id+"F10.opExtrude","SWEPT_FACE",FACE,{"disambiguationData":[OSD([subQ7])]}),makeQuery(id+"F12.opExtrude","CAP_FACE",FACE,{"disambiguationData":[OSD([subQ8])],"isStart":false})]}),makeQuery(id+"F14.opExtrude","CAP_FACE",FACE,{"disambiguationData":[OSD([subQ6,subQ5,subQ4,subQ3,subQ2,subQ1,subQ0])],"isStart":true})]}),makeQuery(id+"F18.opExtrude","CAP_FACE",FACE,{"disambiguationData":[OSD([subQ8,subQ7,subQ6,subQ5,subQ4,subQ3,subQ2,subQ1,subQ0])],"isStart":false})]}),makeQuery(id+"F19.imprint","IMPRINT",EDGE,{"derivedFrom":sQuery(id+"F19.wireOp",EDGE,"E48")})]});}
            var Q12;
            {var subQ0=sQuery(id+"F7.wireOp",EDGE,"E16");var subQ9=makeQuery(id+"F8.opExtrude","SWEPT_FACE",FACE,{"disambiguationData":[OSD([subQ0])]});var subQ10=sQuery(id+"F11.wireOp",EDGE,"E26");Q12=makeQuery(id+"F20.boolean.opBoolean","SPLIT",EDGE,{"disambiguationData":[TD([makeQuery(id+"F20.opExtrude","SWEPT_FACE",FACE,{"disambiguationData":[OSD([sQuery(id+"F19.wireOp",EDGE,"E48")])]})])],"derivedFrom":makeQuery(id+"F12.opExtrude","TWEAK_EDGE",EDGE,{"derivedFrom":[subQ9,makeQuery(id+"F11.imprint","IMPRINT",EDGE,{"derivedFrom":subQ10})]})});}
            var Q13;
            Q13=makeQuery(id+"F10.opExtrude","CAP_EDGE",EDGE,{"disambiguationData":[OSD([sQuery(id+"F9.wireOp",EDGE,"E21")])],"isStart":false});
            var Q14;
            Q14=makeQuery(id+"F30.opExtrude","CAP_EDGE",EDGE,{"disambiguationData":[OSD([sQuery(id+"F29.wireOp",EDGE,"E62")])],"isStart":true});
            var Q15;
            Q15=makeQuery(id+"F30.opExtrude","CAP_EDGE",EDGE,{"disambiguationData":[OSD([sQuery(id+"F29.wireOp",EDGE,"E61")])],"isStart":false});
            var Q16;
            Q16=makeQuery(id+"F30.boolean.opBoolean","INTERSECT",EDGE,{"derivedFrom":[makeQuery(id+"F20.boolean.opBoolean","SPLIT",FACE,{"disambiguationData":[TD([makeQuery(id+"F20.opExtrude","SWEPT_FACE",FACE,{"disambiguationData":[OSD([sQuery(id+"F19.wireOp",EDGE,"E48")])]})])],"derivedFrom":makeQuery(id+"F12.opExtrude","SWEPT_FACE",FACE,{"disambiguationData":[OSD([sQuery(id+"F11.wireOp",EDGE,"E26")])]})}),makeQuery(id+"F30.opExtrude","CAP_FACE",FACE,{"disambiguationData":[OSD([sQuery(id+"F29.wireOp",EDGE,"E61"),sQuery(id+"F29.wireOp",EDGE,"E62"),sQuery(id+"F29.wireOp",EDGE,"E63")])],"isStart":false})]});
            var Q17;
            Q17=makeQuery(id+"F30.opExtrude","CAP_EDGE",EDGE,{"disambiguationData":[OSD([sQuery(id+"F29.wireOp",EDGE,"E62")])],"isStart":false});
            var Q18;
            {var subQ0=sQuery(id+"F15.wireOp",EDGE,"E38.0.2");var subQ1=sQuery(id+"F15.wireOp",EDGE,"E37.0");var subQ2=sQuery(id+"F15.wireOp",EDGE,"uAtuuOPQ-Y4R9-PvW4-TTvW-OnEqOC83DOFm");var subQ3=sQuery(id+"F15.wireOp",EDGE,"E36");var subQ4=sQuery(id+"F15.wireOp",EDGE,"E35");var subQ5=sQuery(id+"F9.wireOp",EDGE,"E23");var subQ6=sQuery(id+"F7.wireOp",EDGE,"E18");Q18=makeQuery(id+"F20.opExtrude","TWEAK_EDGE",EDGE,{"derivedFrom":[makeQuery(id+"F18.boolean.opBoolean","MERGE",FACE,{"derivedFrom":[makeQuery(id+"F16.boolean.opBoolean","MERGE",FACE,{"derivedFrom":[makeQuery(id+"F8.opExtrude","SWEPT_FACE",FACE,{"disambiguationData":[OSD([subQ6])]}),makeQuery(id+"F12.boolean.opBoolean","MERGE",FACE,{"derivedFrom":[makeQuery(id+"F10.opExtrude","SWEPT_FACE",FACE,{"disambiguationData":[OSD([subQ5])]}),makeQuery(id+"F12.opExtrude","CAP_FACE",FACE,{"disambiguationData":[OSD([subQ6])],"isStart":true})]}),makeQuery(id+"F16.opExtrude","CAP_FACE",FACE,{"disambiguationData":[OSD([subQ4,subQ3,subQ2,subQ1,subQ0])],"isStart":true})]}),makeQuery(id+"F18.opExtrude","CAP_FACE",FACE,{"disambiguationData":[OSD([subQ6,subQ5,subQ4,subQ3,subQ2,subQ1,subQ0])],"isStart":true})]}),makeQuery(id+"F19.imprint","IMPRINT",EDGE,{"derivedFrom":sQuery(id+"F19.wireOp",EDGE,"E48")})]});}
            var Q19;
            {var subQ6=sQuery(id+"F7.wireOp",EDGE,"E18");var subQ7=makeQuery(id+"F8.opExtrude","SWEPT_FACE",FACE,{"disambiguationData":[OSD([subQ6])]});var subQ8=sQuery(id+"F11.wireOp",EDGE,"E26");Q19=makeQuery(id+"F20.boolean.opBoolean","SPLIT",EDGE,{"disambiguationData":[TD([makeQuery(id+"F12.opExtrude","SWEPT_FACE",FACE,{"disambiguationData":[OSD([sQuery(id+"F11.wireOp",EDGE,"E27")])]})])],"derivedFrom":makeQuery(id+"F12.opExtrude","TWEAK_EDGE",EDGE,{"derivedFrom":[subQ7,makeQuery(id+"F11.imprint","IMPRINT",EDGE,{"derivedFrom":subQ8})]})});}
            var Q20;
            {var subQ7=sQuery(id+"F7.wireOp",EDGE,"E16");var subQ8=makeQuery(id+"F8.opExtrude","SWEPT_FACE",FACE,{"disambiguationData":[OSD([subQ7])]});var subQ10=sQuery(id+"F11.wireOp",EDGE,"E26");Q20=makeQuery(id+"F20.boolean.opBoolean","SPLIT",EDGE,{"disambiguationData":[TD([makeQuery(id+"F12.opExtrude","SWEPT_FACE",FACE,{"disambiguationData":[OSD([sQuery(id+"F11.wireOp",EDGE,"E27")])]})])],"derivedFrom":makeQuery(id+"F12.opExtrude","TWEAK_EDGE",EDGE,{"derivedFrom":[subQ8,makeQuery(id+"F11.imprint","IMPRINT",EDGE,{"derivedFrom":subQ10})]})});}
            var Q21;
            {var subQ0=sQuery(id+"F7.wireOp",EDGE,"E19");Q21=makeQuery(id+"F8.opExtrude","CAP_EDGE",EDGE,{"disambiguationData":[OSD([subQ0]),TDD([makeQuery(id+"F7.imprint","IMPRINT",EDGE,{"disambiguationData":[TD([[makeQuery(id+"F7.imprint","INTERSECT",VERTEX,{"derivedFrom":[sQuery(id+"F7.wireOp",EDGE,"E17"),subQ0]}),1.0]])],"derivedFrom":subQ0})])],"isStart":false});}
            var Q22;
            Q22=makeQuery(id+"F10.opExtrude","CAP_EDGE",EDGE,{"disambiguationData":[OSD([sQuery(id+"F9.wireOp",EDGE,"E20")])],"isStart":false});
            var Q23;
            Q23=makeQuery(id+"F10.opExtrude","CAP_EDGE",EDGE,{"disambiguationData":[OSD([sQuery(id+"F9.wireOp",EDGE,"E23")])],"isStart":false});
            var Q24;
            {var subQ0=sQuery(id+"F7.wireOp",EDGE,"E18");var subQ7=makeQuery(id+"F8.opExtrude","SWEPT_FACE",FACE,{"disambiguationData":[OSD([subQ0])]});var subQ8=sQuery(id+"F11.wireOp",EDGE,"E26");Q24=makeQuery(id+"F20.boolean.opBoolean","SPLIT",EDGE,{"disambiguationData":[TD([makeQuery(id+"F20.opExtrude","SWEPT_FACE",FACE,{"disambiguationData":[OSD([sQuery(id+"F19.wireOp",EDGE,"E48")])]})])],"derivedFrom":makeQuery(id+"F12.opExtrude","TWEAK_EDGE",EDGE,{"derivedFrom":[subQ7,makeQuery(id+"F11.imprint","IMPRINT",EDGE,{"derivedFrom":subQ8})]})});}
            var Q25;
            Q25=makeQuery(id+"F10.opExtrude","CAP_FACE",FACE,{"disambiguationData":[OSD([sQuery(id+"F9.wireOp",EDGE,"E20"),sQuery(id+"F9.wireOp",EDGE,"E21"),sQuery(id+"F9.wireOp",EDGE,"E22"),sQuery(id+"F9.wireOp",EDGE,"E23")])],"isStart":false});
            var Q26;
            Q26=makeQuery(id+"F33.boolean.opBoolean","COPY",EDGE,{"derivedFrom":makeQuery(id+"F33.opExtrude","CAP_EDGE",EDGE,{"disambiguationData":[OSD([sQuery(id+"F32.wireOp",EDGE,"E64.bottom")])],"isStart":false})});
            var Q27;
            Q27=makeQuery(id+"F33.boolean.opBoolean","COPY",EDGE,{"derivedFrom":makeQuery(id+"F33.opExtrude","CAP_EDGE",EDGE,{"disambiguationData":[OSD([sQuery(id+"F32.wireOp",EDGE,"E64.right")])],"isStart":false})});
            var Q28;
            Q28=makeQuery(id+"F33.boolean.opBoolean","COPY",EDGE,{"derivedFrom":makeQuery(id+"F33.opExtrude","SWEPT_EDGE",EDGE,{"disambiguationData":[OSD([sQuery(id+"F32.wireOp",EDGE,"E64.bottom"),sQuery(id+"F32.wireOp",EDGE,"E64.right")])]})});
            var Q29;
            Q29=makeQuery(id+"F33.boolean.opBoolean","COPY",EDGE,{"derivedFrom":makeQuery(id+"F33.opExtrude","CAP_EDGE",EDGE,{"disambiguationData":[OSD([sQuery(id+"F32.wireOp",EDGE,"E64.top")])],"isStart":false})});
            var Q30;
            Q30=makeQuery(id+"F33.boolean.opBoolean","COPY",EDGE,{"derivedFrom":makeQuery(id+"F33.opExtrude","CAP_EDGE",EDGE,{"disambiguationData":[OSD([sQuery(id+"F32.wireOp",EDGE,"E64.left")])],"isStart":false})});
            var Q31;
            Q31=makeQuery(id+"F33.boolean.opBoolean","COPY",EDGE,{"derivedFrom":makeQuery(id+"F33.opExtrude","SWEPT_EDGE",EDGE,{"disambiguationData":[OSD([sQuery(id+"F32.wireOp",EDGE,"E64.top"),sQuery(id+"F32.wireOp",EDGE,"E64.left")])]})});
            var Q32;
            Q32=makeQuery(id+"F33.boolean.opBoolean","COPY",EDGE,{"derivedFrom":makeQuery(id+"F33.opExtrude","SWEPT_EDGE",EDGE,{"disambiguationData":[OSD([sQuery(id+"F32.wireOp",EDGE,"E64.top"),sQuery(id+"F32.wireOp",EDGE,"E64.right")])]})});
            var Q33;
            Q33=makeQuery(id+"F33.boolean.opBoolean","COPY",EDGE,{"derivedFrom":makeQuery(id+"F33.opExtrude","SWEPT_EDGE",EDGE,{"disambiguationData":[OSD([sQuery(id+"F32.wireOp",EDGE,"E64.bottom"),sQuery(id+"F32.wireOp",EDGE,"E64.left")])]})});
            fillet(context, id + "F34", {"entities" : qUnion([Q0, Q1, Q2, Q3, Q4, Q5, Q6, Q7, Q8, Q9, Q10, Q11, Q12, Q13, Q14, Q15, Q16, Q17, Q18, Q19, Q20, Q21, Q22, Q23, Q24, Q25, Q26, Q27, Q28, Q29, Q30, Q31, Q32, Q33]), "radius" : 1.5 * mm, "tangentPropagation" : true, "allowEdgeOverflow" : false});
        }
        {
            var Q0;
            Q0=makeQuery(id+"F20.opExtrude","SWEPT_FACE",FACE,{"disambiguationData":[OSD([sQuery(id+"F19.wireOp",EDGE,"E48")])]});
            var sketch = newSketch(context, id + "F35", { "sketchPlane" : qUnion([Q0])});
            skPoint(sketch, "E65", {"position": v(-10, -34) * mm});
            skPoint(sketch, "E66.MirrorP", {"position": v(10, -34) * mm});
            skSolve(sketch);
        }
        {
            var Q0;
            Q0=sQuery(id+"F35.wireOp",VERTEX,"E65");
            var Q1;
            Q1=sQuery(id+"F35.wireOp",VERTEX,"E66.MirrorP");
            var Q2;
            Q2=makeQuery(id+"F1.opExtrude","SWEPT_BODY",BODY,{"disambiguationData":[OSD([sQuery(id+"F0.wireOp",EDGE,"E0"),sQuery(id+"F0.wireOp",EDGE,"E1")])]});
            hole(context, id + "F36", {"style" : HoleStyle.SIMPLE, "endStyle" : HoleEndStyle.BLIND, "standardTappedOrClearance" : lookupTablePath({ "standard" : "ISO", "fit" : "Normal", "size" : "M4", "type" : "Clearance" }), "standardBlindInLast" : lookupTablePath({ "fit" : "Standard", "standard" : "ISO", "size" : "M4", "type" : "Clearance" }), "holeDiameter" : 4.4 * mm, "majorDiameter" : 5 * mm, "holeDepth" : 10 * mm, "isTappedThrough" : true, "tappedDepth" : 12 * mm, "tapClearance" : 3, "locations" : qUnion([Q0, Q1]), "scope" : qUnion([Q2])});
        }
    });
